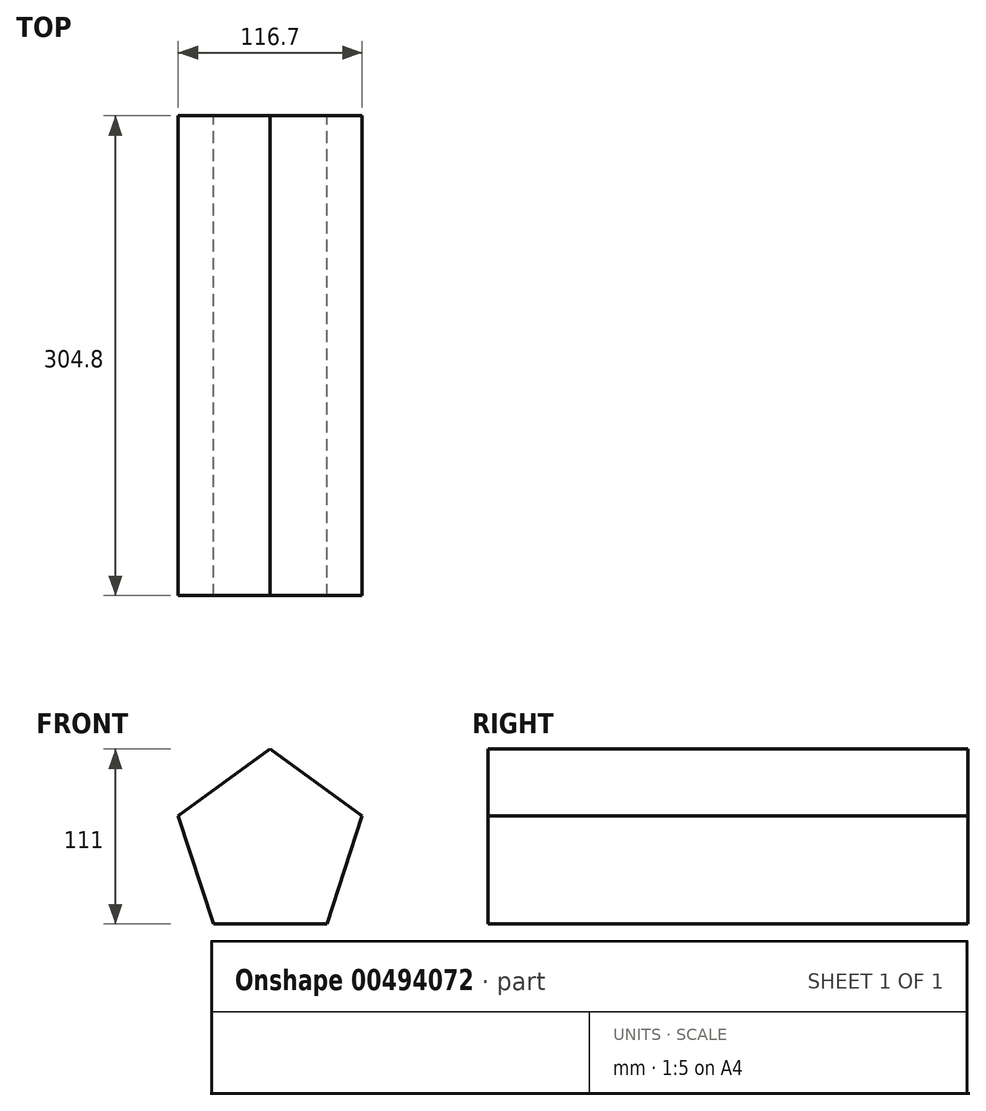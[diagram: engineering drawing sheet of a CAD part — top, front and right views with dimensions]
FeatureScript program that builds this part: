
annotation { "Feature Type Name" : "Feature", "Feature Type Description" : "" }
export const myFeature = defineFeature(function(context is Context, id is Id, definition is map)
    precondition{}
    {
        {
            var Q0;
            Q0=qCreatedBy(makeId("Front.planeOp"),FACE);
            var sketch = newSketch(context, id + "F0", { "sketchPlane" : qUnion([Q0])});
            skCircle(sketch, "E0.cCircle", {"center": v(0, 0) * mm, "radius": 61.36 * mm, "construction": true});
            skLineSegment(sketch, "E0.0", {"start": v(-58.35, 18.96) * mm, "end": v(0, 61.36) * mm});
            skLineSegment(sketch, "E0.1", {"start": v(0, 61.36) * mm, "end": v(58.35, 18.96) * mm});
            skLineSegment(sketch, "E0.2", {"start": v(58.35, 18.96) * mm, "end": v(36.06, -49.64) * mm});
            skLineSegment(sketch, "E0.3", {"start": v(36.06, -49.64) * mm, "end": v(-36.06, -49.64) * mm});
            skLineSegment(sketch, "E0.4", {"start": v(-36.06, -49.64) * mm, "end": v(-58.35, 18.96) * mm});
            skSolve(sketch);
        }
        {
            var Q0;
            Q0=makeQuery(id+"F0.imprint","IMPRINT",FACE,{"disambiguationData":[TD([[makeQuery(id+"F0.imprint","IMPRINT",EDGE,{"derivedFrom":sQuery(id+"F0.wireOp",EDGE,"E0.0")}),-1.0]])]});
            extrude(context, id + "F1", {"entities" : qUnion([Q0]), "depth" : 304.8 * mm});
        }
    });
